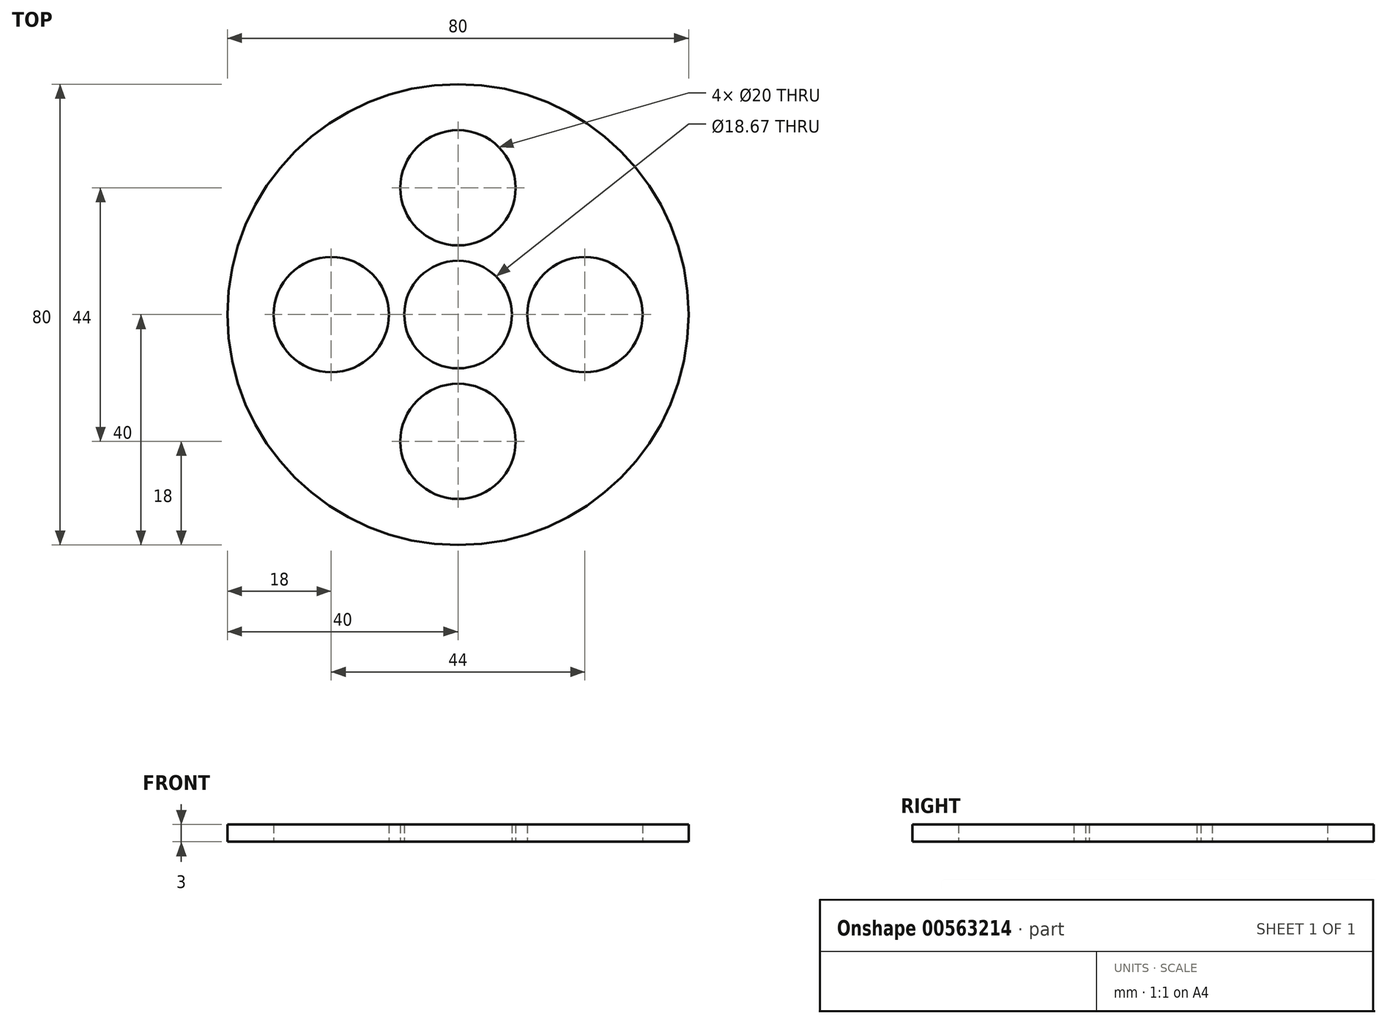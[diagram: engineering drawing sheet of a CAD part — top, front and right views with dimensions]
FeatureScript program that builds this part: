
annotation { "Feature Type Name" : "Feature", "Feature Type Description" : "" }
export const myFeature = defineFeature(function(context is Context, id is Id, definition is map)
    precondition{}
    {
        {
            var Q0;
            Q0=qCreatedBy(makeId("Top.planeOp"),FACE);
            var sketch = newSketch(context, id + "F0", { "sketchPlane" : qUnion([Q0])});
            skCircle(sketch, "E0", {"center": v(0, 0) * mm, "radius": 40 * mm});
            skCircle(sketch, "E1", {"center": v(0, 0) * mm, "radius": 9.33 * mm});
            skCircle(sketch, "E2", {"center": v(0, 22) * mm, "radius": 10 * mm});
            skCircle(sketch, "E3", {"center": v(22, 0) * mm, "radius": 10 * mm});
            skCircle(sketch, "E4", {"center": v(0, -22) * mm, "radius": 10 * mm});
            skCircle(sketch, "E5", {"center": v(-22, 0) * mm, "radius": 10 * mm});
            skSolve(sketch);
        }
        {
            var Q0;
            Q0=qSketchRegion(id+"F0",true);
            extrude(context, id + "F1", {"entities" : qUnion([Q0]), "endBound" : BoundingType.SYMMETRIC, "depth" : 3 * mm, "offsetDistance" : 25 * mm});
        }
    });
